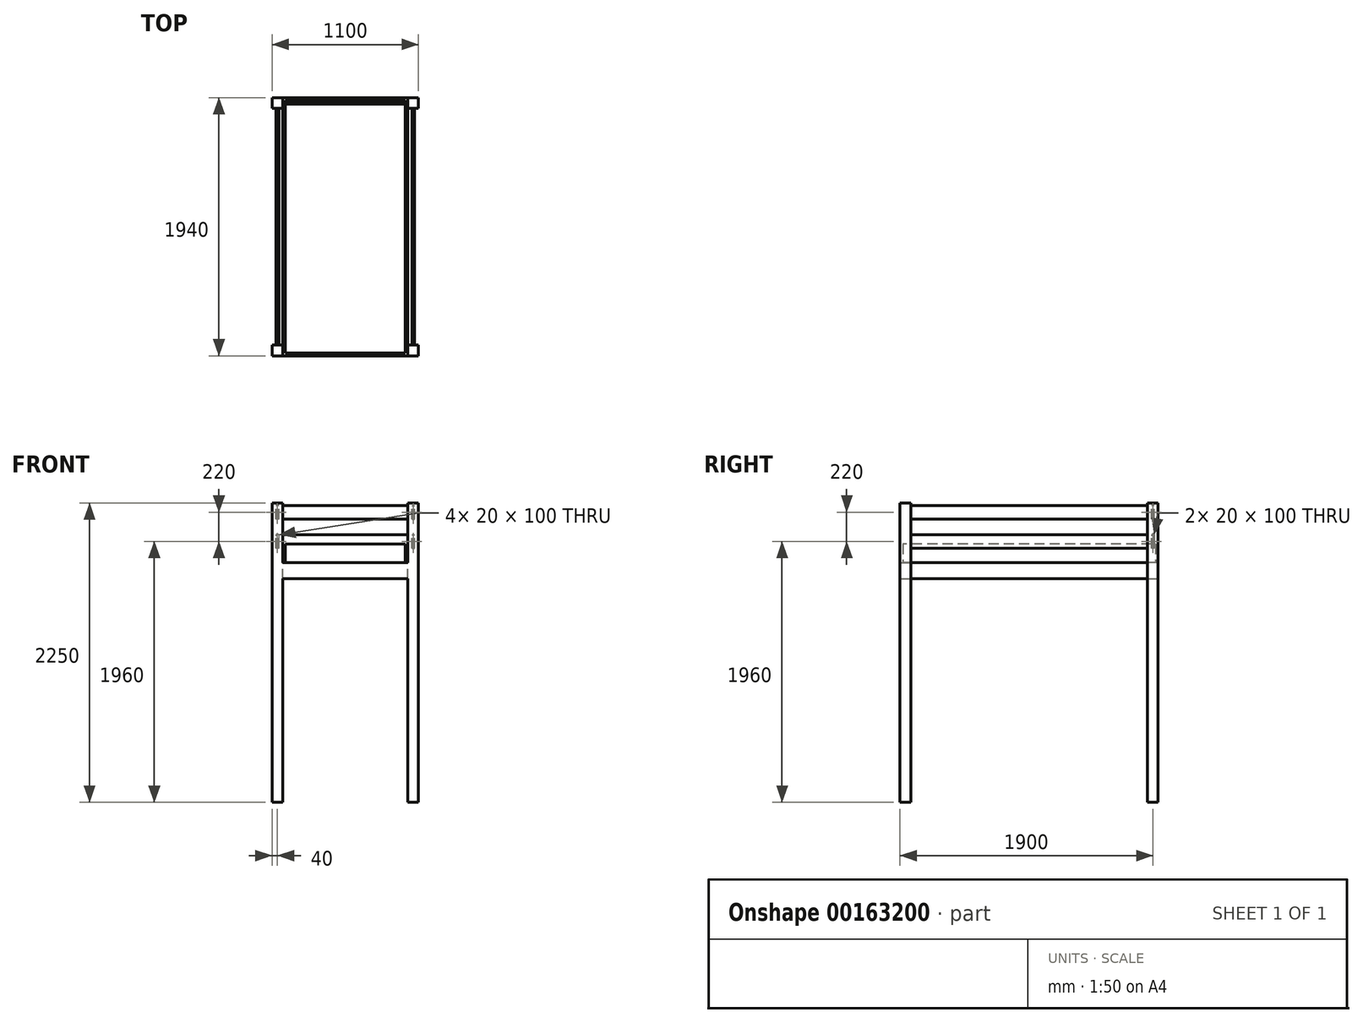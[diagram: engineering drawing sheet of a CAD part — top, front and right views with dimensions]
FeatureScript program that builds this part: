
annotation { "Feature Type Name" : "Feature", "Feature Type Description" : "" }
export const myFeature = defineFeature(function(context is Context, id is Id, definition is map)
    precondition{}
    {
        {
            var Q0;
            Q0=qCreatedBy(makeId("Top.planeOp"),FACE);
            var sketch = newSketch(context, id + "F0", { "sketchPlane" : qUnion([Q0])});
            skLineSegment(sketch, "E0.bottom", {"start": v(-450, 950) * mm, "end": v(450, 950) * mm});
            skLineSegment(sketch, "E0.top", {"start": v(-450, -950) * mm, "end": v(450, -950) * mm});
            skLineSegment(sketch, "E0.left", {"start": v(-450, 950) * mm, "end": v(-450, -950) * mm});
            skLineSegment(sketch, "E0.right", {"start": v(450, 950) * mm, "end": v(450, -950) * mm});
            skPoint(sketch, "E0.middle", {"position": v(0, 0) * mm});
            skSolve(sketch);
        }
        {
            var Q0;
            Q0 = qSketchRegion(id + "F0", true);
            extrude(context, id + "F1", {"entities" : qUnion([Q0]), "depth" : 140 * mm});
        }
        {
            var Q0;
            Q0=makeQuery(id+"F1.opExtrude","CAP_FACE",FACE,{"disambiguationData":[OSD([sQuery(id+"F0.wireOp",EDGE,"E0.bottom"),sQuery(id+"F0.wireOp",EDGE,"E0.top"),sQuery(id+"F0.wireOp",EDGE,"E0.left"),sQuery(id+"F0.wireOp",EDGE,"E0.right")])],"isStart":true});
            var sketch = newSketch(context, id + "F2", { "sketchPlane" : qUnion([Q0])});
            skLineSegment(sketch, "E1.0", {"start": v(-470, -970) * mm, "end": v(470, -970) * mm});
            skLineSegment(sketch, "E1.1", {"start": v(-470, 970) * mm, "end": v(-470, -970) * mm});
            skLineSegment(sketch, "E1.2", {"start": v(470, 970) * mm, "end": v(-470, 970) * mm});
            skLineSegment(sketch, "E1.3", {"start": v(470, -970) * mm, "end": v(470, 970) * mm});
            skSolve(sketch);
        }
        {
            var Q0;
            Q0 = qSketchRegion(id + "F2", true);
            extrude(context, id + "F3", {"entities" : qUnion([Q0]), "depth" : 120 * mm});
        }
        {
            var Q0;
            Q0=makeQuery(id+"F3.opExtrude","CAP_FACE",FACE,{"disambiguationData":[OSD([sQuery(id+"F2.wireOp",EDGE,"E1.0"),sQuery(id+"F2.wireOp",EDGE,"E1.1"),sQuery(id+"F2.wireOp",EDGE,"E1.2"),sQuery(id+"F2.wireOp",EDGE,"E1.3")])],"isStart":true});
            var sketch = newSketch(context, id + "F4", { "sketchPlane" : qUnion([Q0])});
            skLineSegment(sketch, "E2.bottom", {"start": v(470, 970) * mm, "end": v(550, 970) * mm});
            skLineSegment(sketch, "E2.top", {"start": v(470, 890) * mm, "end": v(550, 890) * mm});
            skLineSegment(sketch, "E2.left", {"start": v(470, 970) * mm, "end": v(470, 890) * mm});
            skLineSegment(sketch, "E2.right", {"start": v(550, 970) * mm, "end": v(550, 890) * mm});
            skLineSegment(sketch, "E3.MirrorCS", {"start": v(470, -970) * mm, "end": v(470, -890) * mm});
            skLineSegment(sketch, "E4.MirrorCS", {"start": v(550, -970) * mm, "end": v(550, -890) * mm});
            skLineSegment(sketch, "E5.MirrorCS", {"start": v(470, -890) * mm, "end": v(550, -890) * mm});
            skLineSegment(sketch, "E6.MirrorCS", {"start": v(470, -970) * mm, "end": v(550, -970) * mm});
            skLineSegment(sketch, "E7.MirrorCS", {"start": v(-470, 970) * mm, "end": v(-470, 890) * mm});
            skLineSegment(sketch, "E8.MirrorCS", {"start": v(-470, 970) * mm, "end": v(-550, 970) * mm});
            skLineSegment(sketch, "E9.MirrorCS", {"start": v(-470, -970) * mm, "end": v(-470, -890) * mm});
            skLineSegment(sketch, "E10.MirrorCS", {"start": v(-550, -970) * mm, "end": v(-550, -890) * mm});
            skLineSegment(sketch, "E11.MirrorCS", {"start": v(-470, 890) * mm, "end": v(-550, 890) * mm});
            skLineSegment(sketch, "E12.MirrorCS", {"start": v(-470, -970) * mm, "end": v(-550, -970) * mm});
            skLineSegment(sketch, "E13.MirrorCS", {"start": v(-550, 970) * mm, "end": v(-550, 890) * mm});
            skLineSegment(sketch, "E14.MirrorCS", {"start": v(-470, -890) * mm, "end": v(-550, -890) * mm});
            skSolve(sketch);
        }
        {
            var Q0;
            Q0 = qSketchRegion(id + "F4", true);
            extrude(context, id + "F5", {"entities" : qUnion([Q0]), "operationType" : NewBodyOperationType.ADD, "oppositeDirection" : true, "depth" : 1800 * mm});
        }
        {
            var Q0;
            Q0 = qSketchRegion(id + "F4", true);
            extrude(context, id + "F6", {"entities" : qUnion([Q0]), "operationType" : NewBodyOperationType.ADD, "depth" : 450 * mm});
        }
        {
            var Q0;
            {var subQ0=sQuery(id+"F4.wireOp",EDGE,"E2.right");Q0=makeQuery(id+"F6.boolean.opBoolean","MERGE",FACE,{"derivedFrom":[makeQuery(id+"F5.opExtrude","SWEPT_FACE",FACE,{"disambiguationData":[OSD([subQ0])]}),makeQuery(id+"F6.opExtrude","SWEPT_FACE",FACE,{"disambiguationData":[OSD([subQ0])]})]});}
            var Q1;
            Q1=makeQuery(id+"F6.opExtrude","SWEPT_FACE",FACE,{"disambiguationData":[OSD([sQuery(id+"F4.wireOp",EDGE,"E2.left")])]});
            cPlane(context, id + "F7", {"entities" : qUnion([Q0, Q1]), "cplaneType" : CPlaneType.MID_PLANE, "offset" : 25 * mm, "width" : 150 * mm, "height" : 150 * mm});
        }
        {
            var Q0;
            Q0=qCreatedBy(id+"F7.planeOp",FACE);
            var sketch = newSketch(context, id + "F8", { "sketchPlane" : qUnion([Q0])});
            skLineSegment(sketch, "E15.bottom", {"start": v(970, 430) * mm, "end": v(-970, 430) * mm});
            skLineSegment(sketch, "E15.top", {"start": v(970, 330) * mm, "end": v(-970, 330) * mm});
            skLineSegment(sketch, "E15.left", {"start": v(970, 430) * mm, "end": v(970, 330) * mm});
            skLineSegment(sketch, "E15.right", {"start": v(-970, 430) * mm, "end": v(-970, 330) * mm});
            skLineSegment(sketch, "E16.bottom", {"start": v(970, 210) * mm, "end": v(-970, 210) * mm});
            skLineSegment(sketch, "E16.top", {"start": v(970, 110) * mm, "end": v(-970, 110) * mm});
            skLineSegment(sketch, "E16.left", {"start": v(970, 210) * mm, "end": v(970, 110) * mm});
            skLineSegment(sketch, "E16.right", {"start": v(-970, 210) * mm, "end": v(-970, 110) * mm});
            skSolve(sketch);
        }
        {
            var Q0;
            Q0 = qSketchRegion(id + "F8", true);
            extrude(context, id + "F9", {"entities" : qUnion([Q0]), "endBound" : BoundingType.SYMMETRIC, "depth" : 20 * mm});
        }
        {
            var Q0;
            Q0=makeQuery(id+"F9.opExtrude","SWEPT_BODY",BODY,{"disambiguationData":[OSD([sQuery(id+"F8.wireOp",EDGE,"E16.bottom"),sQuery(id+"F8.wireOp",EDGE,"E16.top"),sQuery(id+"F8.wireOp",EDGE,"E16.left"),sQuery(id+"F8.wireOp",EDGE,"E16.right")])]});
            var Q1;
            Q1=makeQuery(id+"F9.opExtrude","SWEPT_BODY",BODY,{"disambiguationData":[OSD([sQuery(id+"F8.wireOp",EDGE,"E15.bottom"),sQuery(id+"F8.wireOp",EDGE,"E15.top"),sQuery(id+"F8.wireOp",EDGE,"E15.left"),sQuery(id+"F8.wireOp",EDGE,"E15.right")])]});
            var Q2;
            Q2=qCreatedBy(makeId("Right.planeOp"),FACE);
            mirror(context, id + "F10", {"operationType" : NewBodyOperationType.ADD, "entities" : qUnion([Q0, Q1]), "mirrorPlane" : qUnion([Q2])});
        }
        {
            var Q0;
            {var subQ0=sQuery(id+"F4.wireOp",EDGE,"E8.MirrorCS");var subQ1=sQuery(id+"F4.wireOp",EDGE,"E2.bottom");Q0=makeQuery(id+"F6.boolean.opBoolean","MERGE",FACE,{"derivedFrom":[makeQuery(id+"F5.boolean.opBoolean","MERGE",FACE,{"derivedFrom":[makeQuery(id+"F3.opExtrude","SWEPT_FACE",FACE,{"disambiguationData":[OSD([sQuery(id+"F2.wireOp",EDGE,"E1.0")])]}),makeQuery(id+"F5.opExtrude","SWEPT_FACE",FACE,{"disambiguationData":[OSD([subQ1])]}),makeQuery(id+"F5.opExtrude","SWEPT_FACE",FACE,{"disambiguationData":[OSD([subQ0])]})]}),makeQuery(id+"F6.opExtrude","SWEPT_FACE",FACE,{"disambiguationData":[OSD([subQ1])]}),makeQuery(id+"F6.opExtrude","SWEPT_FACE",FACE,{"disambiguationData":[OSD([subQ0])]})]});}
            var Q1;
            {var subQ0=sQuery(id+"F4.wireOp",EDGE,"E2.top");Q1=makeQuery(id+"F6.boolean.opBoolean","MERGE",FACE,{"derivedFrom":[makeQuery(id+"F5.opExtrude","SWEPT_FACE",FACE,{"disambiguationData":[OSD([subQ0])]}),makeQuery(id+"F6.opExtrude","SWEPT_FACE",FACE,{"disambiguationData":[OSD([subQ0])]})]});}
            cPlane(context, id + "F11", {"entities" : qUnion([Q0, Q1]), "cplaneType" : CPlaneType.MID_PLANE, "offset" : 25 * mm, "width" : 150 * mm, "height" : 150 * mm});
        }
        {
            var Q0;
            Q0=qCreatedBy(id+"F11.planeOp",FACE);
            var sketch = newSketch(context, id + "F12", { "sketchPlane" : qUnion([Q0])});
            skLineSegment(sketch, "E17.bottom", {"start": v(-520, 430) * mm, "end": v(520, 430) * mm});
            skLineSegment(sketch, "E17.top", {"start": v(-520, 330) * mm, "end": v(520, 330) * mm});
            skLineSegment(sketch, "E17.left", {"start": v(-520, 430) * mm, "end": v(-520, 330) * mm});
            skLineSegment(sketch, "E17.right", {"start": v(520, 430) * mm, "end": v(520, 330) * mm});
            skLineSegment(sketch, "E18.bottom", {"start": v(-520, 210) * mm, "end": v(520, 210) * mm});
            skLineSegment(sketch, "E18.top", {"start": v(-520, 110) * mm, "end": v(520, 110) * mm});
            skLineSegment(sketch, "E18.left", {"start": v(-520, 210) * mm, "end": v(-520, 110) * mm});
            skLineSegment(sketch, "E18.right", {"start": v(520, 210) * mm, "end": v(520, 110) * mm});
            skSolve(sketch);
        }
        {
            var Q0;
            Q0 = qSketchRegion(id + "F12", true);
            extrude(context, id + "F13", {"entities" : qUnion([Q0]), "operationType" : NewBodyOperationType.ADD, "endBound" : BoundingType.SYMMETRIC, "depth" : 20 * mm});
        }
    });
